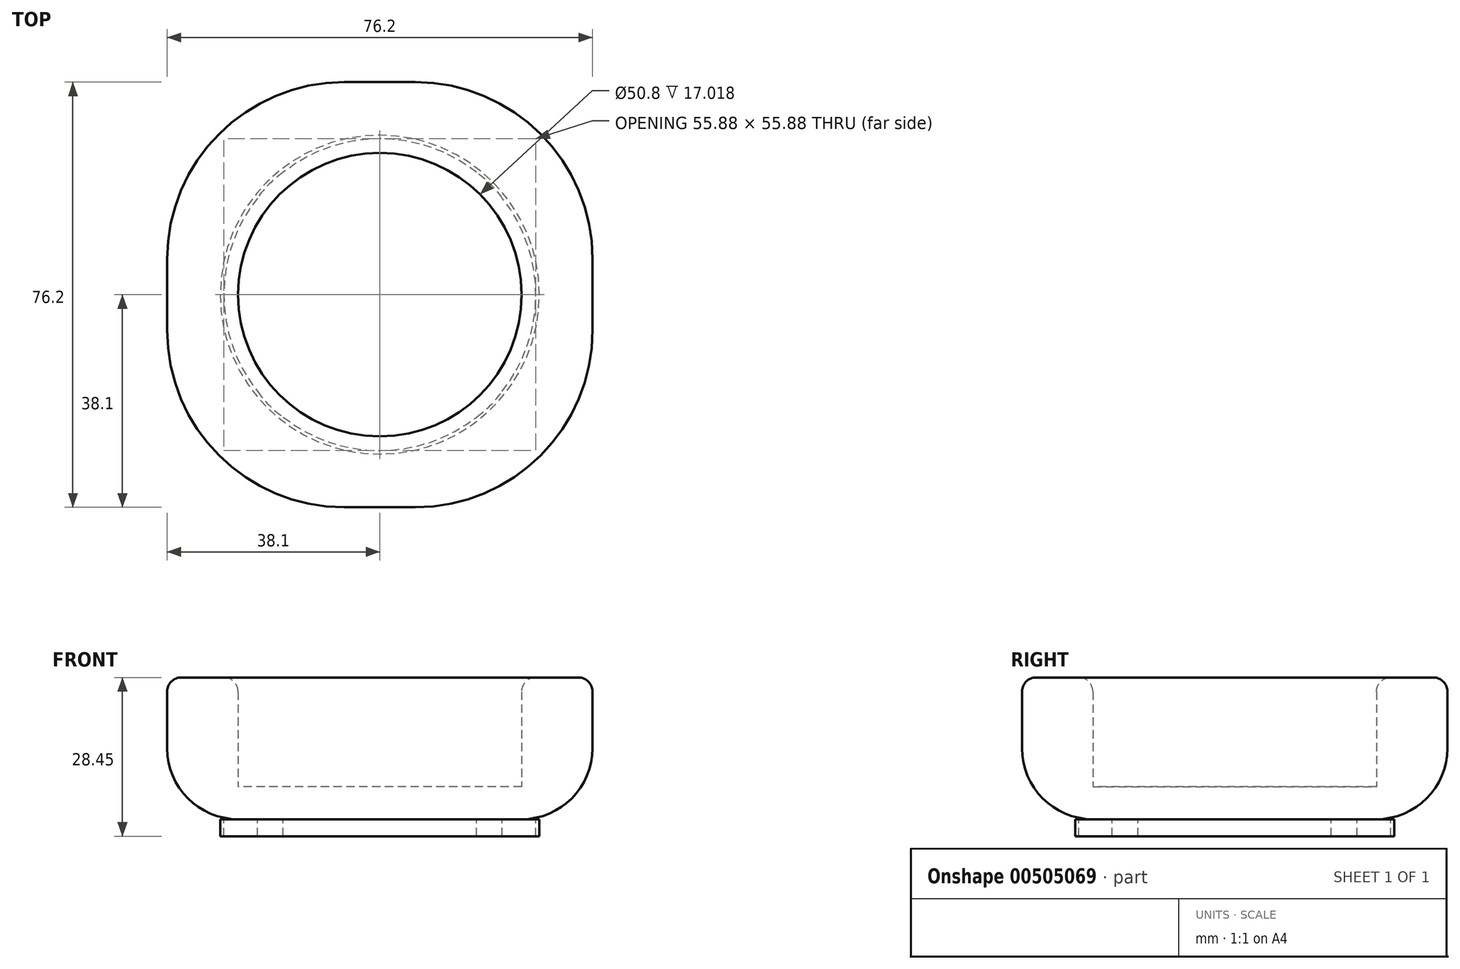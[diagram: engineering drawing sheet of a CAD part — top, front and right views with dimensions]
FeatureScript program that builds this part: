
annotation { "Feature Type Name" : "Feature", "Feature Type Description" : "" }
export const myFeature = defineFeature(function(context is Context, id is Id, definition is map)
    precondition{}
    {
        {
            var Q0;
            Q0=qCreatedBy(makeId("Top.planeOp"),FACE);
            var sketch = newSketch(context, id + "F0", { "sketchPlane" : qUnion([Q0])});
            skLineSegment(sketch, "E0.bottom", {"start": v(38.1, -38.1) * mm, "end": v(-38.1, -38.1) * mm});
            skLineSegment(sketch, "E0.top", {"start": v(38.1, 38.1) * mm, "end": v(-38.1, 38.1) * mm});
            skLineSegment(sketch, "E0.left", {"start": v(38.1, -38.1) * mm, "end": v(38.1, 38.1) * mm});
            skLineSegment(sketch, "E0.right", {"start": v(-38.1, -38.1) * mm, "end": v(-38.1, 38.1) * mm});
            skPoint(sketch, "E0.middle", {"position": v(0, 0) * mm});
            skCircle(sketch, "E1", {"center": v(0, 0) * mm, "radius": 25.4 * mm});
            skSolve(sketch);
        }
        {
            var Q0;
            Q0=makeQuery(id+"F0.imprint","IMPRINT",FACE,{"disambiguationData":[TD([[makeQuery(id+"F0.imprint","IMPRINT",EDGE,{"derivedFrom":sQuery(id+"F0.wireOp",EDGE,"E0.bottom")}),-1.0]])]});
            extrude(context, id + "F1", {"entities" : qUnion([Q0]), "depth" : 25.4 * mm});
        }
        {
            var Q0;
            Q0=makeQuery(id+"F0.imprint","IMPRINT",FACE,{"disambiguationData":[TD([[makeQuery(id+"F0.imprint","IMPRINT",EDGE,{"derivedFrom":sQuery(id+"F0.wireOp",EDGE,"E1")}),1.0]])]});
            extrude(context, id + "F2", {"entities" : qUnion([Q0]), "operationType" : NewBodyOperationType.ADD, "depth" : 5.84 * mm});
        }
        {
            var Q0;
            Q0=makeQuery(id+"F1.opExtrude","SWEPT_EDGE",EDGE,{"disambiguationData":[OSD([sQuery(id+"F0.wireOp",EDGE,"E0.top"),sQuery(id+"F0.wireOp",EDGE,"E0.left")])]});
            var Q1;
            Q1=makeQuery(id+"F1.opExtrude","SWEPT_EDGE",EDGE,{"disambiguationData":[OSD([sQuery(id+"F0.wireOp",EDGE,"E0.top"),sQuery(id+"F0.wireOp",EDGE,"E0.right")])]});
            var Q2;
            Q2=makeQuery(id+"F1.opExtrude","SWEPT_EDGE",EDGE,{"disambiguationData":[OSD([sQuery(id+"F0.wireOp",EDGE,"E0.bottom"),sQuery(id+"F0.wireOp",EDGE,"E0.right")])]});
            var Q3;
            Q3=makeQuery(id+"F1.opExtrude","SWEPT_EDGE",EDGE,{"disambiguationData":[OSD([sQuery(id+"F0.wireOp",EDGE,"E0.bottom"),sQuery(id+"F0.wireOp",EDGE,"E0.left")])]});
            fillet(context, id + "F3", {"entities" : qUnion([Q0, Q1, Q2, Q3]), "radius" : 31.75 * mm, "tangentPropagation" : true, "allowEdgeOverflow" : false});
        }
        {
            var Q0;
            {var subQ0=sQuery(id+"F0.wireOp",EDGE,"E1");Q0=makeQuery(id+"F2.boolean.opBoolean","MERGE",FACE,{"derivedFrom":[makeQuery(id+"F1.opExtrude","CAP_FACE",FACE,{"disambiguationData":[OSD([sQuery(id+"F0.wireOp",EDGE,"E0.bottom"),sQuery(id+"F0.wireOp",EDGE,"E0.top"),sQuery(id+"F0.wireOp",EDGE,"E0.left"),sQuery(id+"F0.wireOp",EDGE,"E0.right"),subQ0])],"isStart":true}),makeQuery(id+"F2.opExtrude","CAP_FACE",FACE,{"disambiguationData":[OSD([subQ0])],"isStart":true})]});}
            fillet(context, id + "F4", {"entities" : qUnion([Q0]), "radius" : 12.7 * mm, "tangentPropagation" : true, "allowEdgeOverflow" : false});
        }
        {
            var Q0;
            Q0=makeQuery(id+"F1.opExtrude","CAP_FACE",FACE,{"disambiguationData":[OSD([sQuery(id+"F0.wireOp",EDGE,"E0.bottom"),sQuery(id+"F0.wireOp",EDGE,"E0.top"),sQuery(id+"F0.wireOp",EDGE,"E0.left"),sQuery(id+"F0.wireOp",EDGE,"E0.right"),sQuery(id+"F0.wireOp",EDGE,"E1")])],"isStart":false});
            fillet(context, id + "F5", {"entities" : qUnion([Q0]), "radius" : 2.54 * mm, "tangentPropagation" : true, "allowEdgeOverflow" : false});
        }
        {
            var Q0;
            {var subQ0=sQuery(id+"F0.wireOp",EDGE,"E1");Q0=makeQuery(id+"F2.boolean.opBoolean","MERGE",FACE,{"derivedFrom":[makeQuery(id+"F1.opExtrude","CAP_FACE",FACE,{"disambiguationData":[OSD([sQuery(id+"F0.wireOp",EDGE,"E0.bottom"),sQuery(id+"F0.wireOp",EDGE,"E0.top"),sQuery(id+"F0.wireOp",EDGE,"E0.left"),sQuery(id+"F0.wireOp",EDGE,"E0.right"),subQ0])],"isStart":true}),makeQuery(id+"F2.opExtrude","CAP_FACE",FACE,{"disambiguationData":[OSD([subQ0])],"isStart":true})]});}
            var sketch = newSketch(context, id + "F6", { "sketchPlane" : qUnion([Q0])});
            skCircle(sketch, "E2", {"center": v(0, 0) * mm, "radius": 28.58 * mm});
            skCircle(sketch, "E3", {"center": v(0, 0) * mm, "radius": 27.94 * mm});
            skSolve(sketch);
        }
        {
            var Q0;
            Q0=makeQuery(id+"F6.imprint","IMPRINT",FACE,{"disambiguationData":[TD([[makeQuery(id+"F6.imprint","IMPRINT",EDGE,{"derivedFrom":sQuery(id+"F6.wireOp",EDGE,"E2")}),1.0]])]});
            extrude(context, id + "F7", {"entities" : qUnion([Q0]), "depth" : 3.05 * mm});
        }
    });
